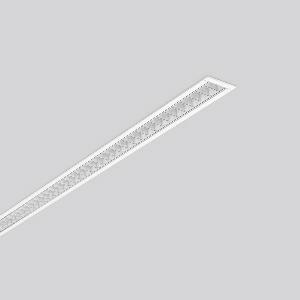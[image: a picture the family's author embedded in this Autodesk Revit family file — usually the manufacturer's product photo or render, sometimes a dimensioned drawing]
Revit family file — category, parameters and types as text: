
# Revit family: less_is_more_27_312177_002_76_6c33
name_source: partatom
category: Lighting Fixtures
units: mm (PartAtom-declared; Revit-internal decimal feet)

## family parameters
Cut with Voids When Loaded = No
Host = Face
Light Source = No
Part Type = Normal
Room Calculation Point = No
Round Connector Dimension = Use Diameter
Shared = No

## types (1)
- LESS IS MORE 27 (1 x LED Modul 830, 2350 lm, 3000)
    Apparent Load = 29 VA
    CIE Flux Codes = 90 99 100 100 100
    Color Rendering = 80
    Color Temperature = 3000
    Default Elevation = 1800 mm
    Description = Series: LESS IS MORE 27
Recessed ceiling and wall luminaire with slim design. Housing: extruded aluminium profile, powder-coated. End cap aluminium powder-coated. High polish aluminium micro grid. Perfect for office areas (RUG < 19) and environments with computer screens in accordance with EN 12464-1. Suitable for Recessed ceiling mounting, wall (recessed). External driver with connecting cable. 
Colour: traffic white, matt (RAL 9016)
Length: 1014 mm
Width: 38 mm
Height: 2 mm
Cut-out length: 1006 mm
Cut-out width: 30 mm
Recess height: 45-60 mm
Luminaire: recess height: 37 mm
Lamp: LED
Socket: without socket
Colour temperature: 3000K
Colour rendering index (CRI): 82
System power: 29 W
Rated luminous flux: 2350 lm
Luminous efficiency: 81 lm/W
Control gear: Voltage converter, DALI dim.
Protection class: II
Type of protection: IP 20
    Height = 0 mm  [stored 0 ft]
    Lamp = 1 x LED Modul 830
    Lamp Light Flux = 2350 lm
    Lamp count = 1
    Length = 1014 mm
    Lifetime = 50000 h
    Luminous efficacy = 81 lm/W
    Manufacturer = RZB
    ModVariant = No
    Model = 312177.002.76
    Mounting Place = Ceiling, Wall
    Mounting Type = Recessed
    Number of Poles = 1
    OnlyDefault = Yes
    Power Factor = 1
    Product Name = LESS IS MORE 27
    Product group = Recessed LED linear luminaires
    ProductGroupID = 407
    Protection Class = Protection class II
    Protection Degree = IP 20
    RLX_Detail_Level = 1
    RLX_Emergency_Light_Flux = 0 lm
    RLX_Emergency_Type = 0
    RLX_Emergency_Type_DB = No
    RlxData = <blob elided: 27005 chars, md5=7fbdb9fa>
    Socket = socket
    Standby Power = 0 W
    System Light Flux = 2350 lm
    System Power = 29 W
    Type Comments = Product without accessories
    Type Image = 312177.002.jpg
    URL = http://relux.com
    VarID = ---
    Voltage = 230 V
    Voltage Range = 220-240 V
    Weight = 0.00 kg
    Width = 38 mm

note: [stored X ft] marks values corroborated as IEEE doubles in the binary element streams (Revit-internal decimal feet)

## geometry (parser evidence)
native form markers: Blend x4, Sweep x14
no freeform markers — native parametric forms only
